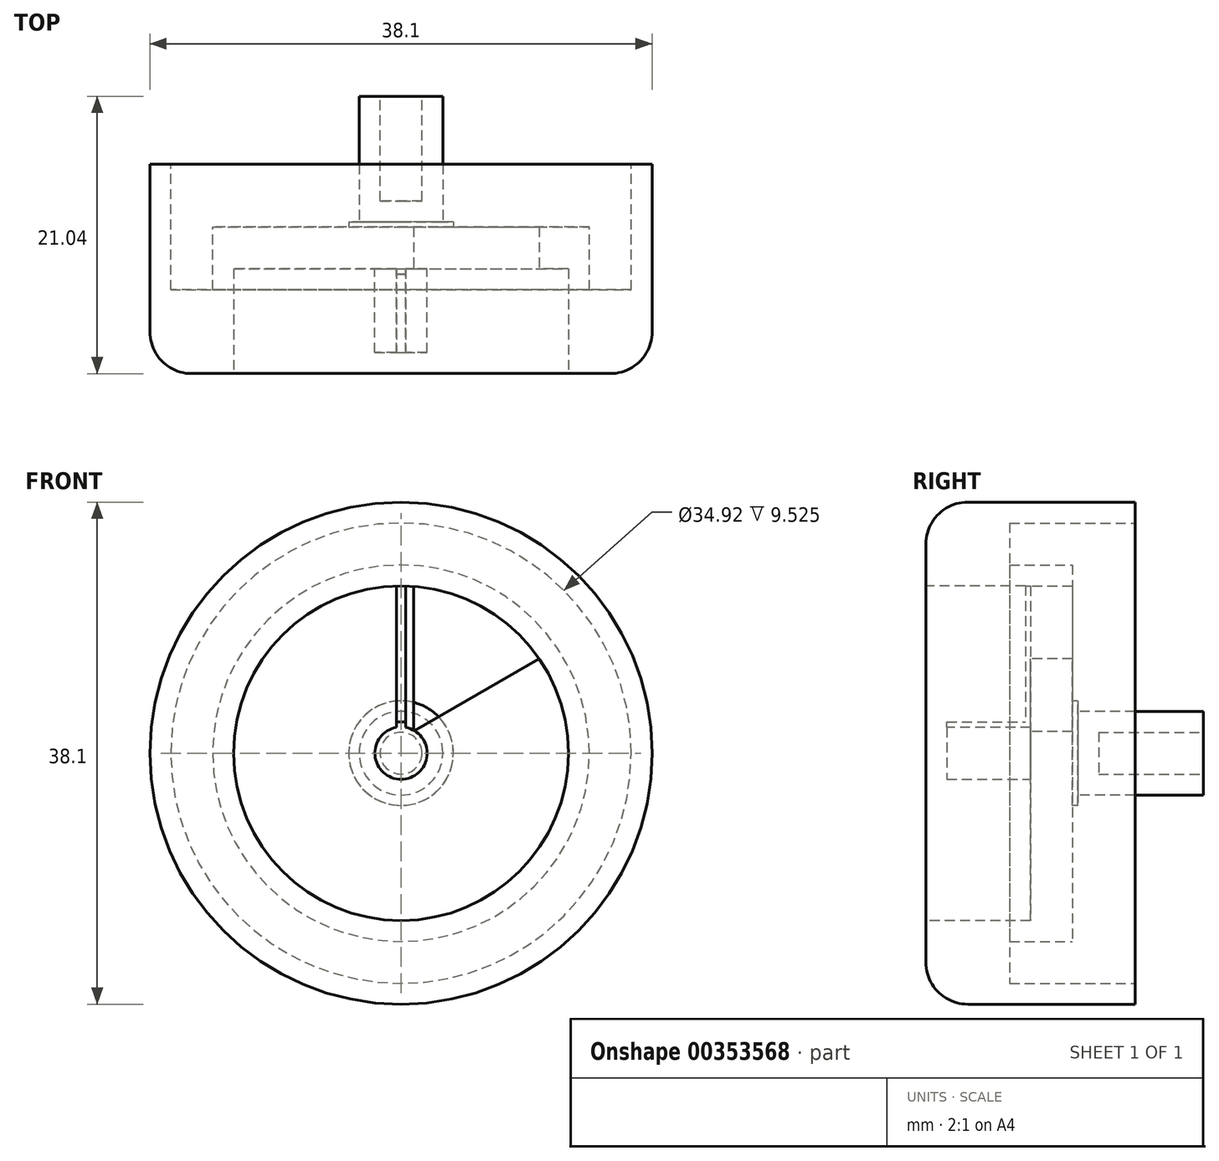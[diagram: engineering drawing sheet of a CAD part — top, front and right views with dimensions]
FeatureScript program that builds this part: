
annotation { "Feature Type Name" : "Feature", "Feature Type Description" : "" }
export const myFeature = defineFeature(function(context is Context, id is Id, definition is map)
    precondition{}
    {
        {
            var Q0;
            Q0=qCreatedBy(makeId("Front.planeOp"),FACE);
            var sketch = newSketch(context, id + "F0", { "sketchPlane" : qUnion([Q0])});
            skCircle(sketch, "E0", {"center": v(0, 0) * mm, "radius": 19.05 * mm});
            skSolve(sketch);
        }
        {
            var Q0;
            Q0 = qSketchRegion(id + "F0", true);
            extrude(context, id + "F1", {"entities" : qUnion([Q0]), "depth" : 15.88 * mm, "symmetric" : true});
        }
        {
            var Q0;
            Q0=makeQuery(id+"F1.opExtrude","CAP_FACE",FACE,{"disambiguationData":[OSD([sQuery(id+"F0.wireOp",EDGE,"E0")])],"isStart":false});
            var sketch = newSketch(context, id + "F2", { "sketchPlane" : qUnion([Q0])});
            skCircle(sketch, "E1", {"center": v(0, 0) * mm, "radius": 12.7 * mm});
            skSolve(sketch);
        }
        {
            var Q0;
            Q0 = qSketchRegion(id + "F2", true);
            extrude(context, id + "F3", {"entities" : qUnion([Q0]), "operationType" : NewBodyOperationType.REMOVE, "oppositeDirection" : true, "depth" : 7.94 * mm});
        }
        {
            var Q0;
            Q0=makeQuery(id+"F3.boolean.opBoolean","COPY",FACE,{"derivedFrom":makeQuery(id+"F3.opExtrude","CAP_FACE",FACE,{"disambiguationData":[OSD([sQuery(id+"F2.wireOp",EDGE,"E1")])],"isStart":false})});
            var sketch = newSketch(context, id + "F4", { "sketchPlane" : qUnion([Q0])});
            skLineSegment(sketch, "E2", {"start": v(0, 13.75) * mm, "end": v(0, 0) * mm, "construction": true});
            skLineSegment(sketch, "E3", {"start": v(0, 0) * mm, "end": v(12.12, 7) * mm, "construction": true});
            skLineSegment(sketch, "E4", {"start": v(0.95, 12.66) * mm, "end": v(0.95, 1.65) * mm});
            skLineSegment(sketch, "E5", {"start": v(0.95, 1.65) * mm, "end": v(10.5, 7.16) * mm});
            skArc(sketch, "E6.0", {"start": v(10.5, 7.16) * mm, "mid": v(6.35, 11) * mm, "end": v(0.95, 12.66) * mm});
            skLineSegment(sketch, "E7", {"start": v(0, 0) * mm, "end": v(9.55, 16.55) * mm, "construction": true});
            skSolve(sketch);
        }
        {
            var Q0;
            Q0 = qSketchRegion(id + "F4", true);
            extrude(context, id + "F5", {"entities" : qUnion([Q0]), "operationType" : NewBodyOperationType.REMOVE, "endBound" : BoundingType.THROUGH_ALL, "oppositeDirection" : true, "depth" : 25.4 * mm});
        }
        {
            var Q0;
            Q0=makeQuery(id+"F1.opExtrude","CAP_FACE",FACE,{"disambiguationData":[OSD([sQuery(id+"F0.wireOp",EDGE,"E0")])],"isStart":true});
            var sketch = newSketch(context, id + "F6", { "sketchPlane" : qUnion([Q0])});
            skCircle(sketch, "E8", {"center": v(0, 0) * mm, "radius": 12.7 * mm});
            skSolve(sketch);
        }
        {
            var Q0;
            Q0 = qSketchRegion(id + "F6", true);
            extrude(context, id + "F7", {"entities" : qUnion([Q0]), "operationType" : NewBodyOperationType.REMOVE, "oppositeDirection" : true, "depth" : 4.76 * mm});
        }
        {
            var Q0;
            Q0=makeQuery(id+"F7.boolean.opBoolean","COPY",FACE,{"derivedFrom":makeQuery(id+"F7.opExtrude","CAP_FACE",FACE,{"disambiguationData":[OSD([sQuery(id+"F6.wireOp",EDGE,"E8")])],"isStart":false})});
            var sketch = newSketch(context, id + "F8", { "sketchPlane" : qUnion([Q0])});
            skCircle(sketch, "E9", {"center": v(0, 0) * mm, "radius": 3.97 * mm});
            skSolve(sketch);
        }
        {
            var Q0;
            Q0 = qSketchRegion(id + "F8", true);
            extrude(context, id + "F9", {"entities" : qUnion([Q0]), "operationType" : NewBodyOperationType.ADD, "depth" : 0.4 * mm});
        }
        {
            var Q0;
            Q0=makeQuery(id+"F9.opExtrude","CAP_FACE",FACE,{"disambiguationData":[OSD([sQuery(id+"F8.wireOp",EDGE,"E9")])],"isStart":false});
            var sketch = newSketch(context, id + "F10", { "sketchPlane" : qUnion([Q0])});
            skCircle(sketch, "E10", {"center": v(0, 0) * mm, "radius": 3.17 * mm});
            skSolve(sketch);
        }
        {
            var Q0;
            Q0 = qSketchRegion(id + "F10", true);
            extrude(context, id + "F11", {"entities" : qUnion([Q0]), "operationType" : NewBodyOperationType.ADD, "depth" : 9.52 * mm});
        }
        {
            var Q0;
            Q0=makeQuery(id+"F11.opExtrude","CAP_FACE",FACE,{"disambiguationData":[OSD([sQuery(id+"F10.wireOp",EDGE,"E10")])],"isStart":false});
            var sketch = newSketch(context, id + "F12", { "sketchPlane" : qUnion([Q0])});
            skCircle(sketch, "E11", {"center": v(0, 0) * mm, "radius": 1.59 * mm});
            skSolve(sketch);
        }
        {
            var Q0;
            Q0 = qSketchRegion(id + "F12", true);
            extrude(context, id + "F13", {"entities" : qUnion([Q0]), "operationType" : NewBodyOperationType.REMOVE, "oppositeDirection" : true, "depth" : 7.94 * mm});
        }
        {
            var Q0;
            Q0=makeQuery(id+"F3.boolean.opBoolean","COPY",FACE,{"derivedFrom":makeQuery(id+"F3.opExtrude","CAP_FACE",FACE,{"disambiguationData":[OSD([sQuery(id+"F2.wireOp",EDGE,"E1")])],"isStart":false})});
            var sketch = newSketch(context, id + "F14", { "sketchPlane" : qUnion([Q0])});
            skCircle(sketch, "E12", {"center": v(0, 0) * mm, "radius": 1.98 * mm});
            skSolve(sketch);
        }
        {
            var Q0;
            Q0 = qSketchRegion(id + "F14", true);
            extrude(context, id + "F15", {"entities" : qUnion([Q0]), "operationType" : NewBodyOperationType.ADD, "depth" : 6.35 * mm});
        }
        {
            var Q0;
            {var subQ2=sQuery(id+"F2.wireOp",EDGE,"E1");Q0=makeQuery(id+"F15.boolean.opBoolean","SPLIT",FACE,{"disambiguationData":[TD([makeQuery(id+"F5.boolean.opBoolean","COPY",FACE,{"derivedFrom":makeQuery(id+"F5.opExtrude","SWEPT_FACE",FACE,{"disambiguationData":[OSD([sQuery(id+"F4.wireOp",EDGE,"E4")])]})})])],"derivedFrom":makeQuery(id+"F3.boolean.opBoolean","COPY",FACE,{"derivedFrom":makeQuery(id+"F3.opExtrude","CAP_FACE",FACE,{"disambiguationData":[OSD([subQ2])],"isStart":false})})});}
            var sketch = newSketch(context, id + "F16", { "sketchPlane" : qUnion([Q0])});
            skLineSegment(sketch, "E13.bottom", {"start": v(-0.34, 12.7) * mm, "end": v(0.34, 12.7) * mm});
            skLineSegment(sketch, "E13.top", {"start": v(-0.34, 2.37) * mm, "end": v(0.34, 2.37) * mm});
            skLineSegment(sketch, "E13.left", {"start": v(-0.34, 12.7) * mm, "end": v(-0.34, 2.37) * mm});
            skLineSegment(sketch, "E13.right", {"start": v(0.34, 12.7) * mm, "end": v(0.34, 2.37) * mm});
            skSolve(sketch);
        }
        {
            var Q0;
            {var subQ0=sQuery(id+"F16.wireOp",EDGE,"E13.left");var subQ1=sQuery(id+"F16.wireOp",EDGE,"E13.top");var subQ2=makeQuery(id+"F16.imprint","INTERSECT",VERTEX,{"derivedFrom":[subQ1,subQ0]});Q0=makeQuery(id+"F16.imprint","IMPRINT",FACE,{"disambiguationData":[TD([[makeQuery(id+"F16.imprint","IMPRINT",EDGE,{"disambiguationData":[TD([[subQ2,-1.0]])],"derivedFrom":subQ1}),1.0]])]});}
            extrude(context, id + "F17", {"entities" : qUnion([Q0]), "operationType" : NewBodyOperationType.ADD, "depth" : 0.4 * mm});
        }
        {
            var Q0;
            Q0=makeQuery(id+"F15.opExtrude","CAP_FACE",FACE,{"disambiguationData":[OSD([sQuery(id+"F14.wireOp",EDGE,"E12")])],"isStart":false});
            var sketch = newSketch(context, id + "F18", { "sketchPlane" : qUnion([Q0])});
            skLineSegment(sketch, "E14.bottom", {"start": v(-0.34, 1.95) * mm, "end": v(0.34, 1.95) * mm});
            skLineSegment(sketch, "E14.top", {"start": v(-0.34, 2.36) * mm, "end": v(0.34, 2.36) * mm});
            skLineSegment(sketch, "E14.left", {"start": v(-0.34, 1.95) * mm, "end": v(-0.34, 2.36) * mm});
            skLineSegment(sketch, "E14.right", {"start": v(0.34, 1.95) * mm, "end": v(0.34, 2.36) * mm});
            skSolve(sketch);
        }
        {
            var Q0;
            Q0 = qSketchRegion(id + "F18", true);
            extrude(context, id + "F19", {"entities" : qUnion([Q0]), "operationType" : NewBodyOperationType.ADD, "oppositeDirection" : true, "depth" : 6.35 * mm});
        }
        {
            var Q0;
            Q0=makeQuery(id+"F1.opExtrude","CAP_FACE",FACE,{"disambiguationData":[OSD([sQuery(id+"F0.wireOp",EDGE,"E0")])],"isStart":true});
            var sketch = newSketch(context, id + "F20", { "sketchPlane" : qUnion([Q0])});
            skCircle(sketch, "E15", {"center": v(0, 0) * mm, "radius": 17.46 * mm});
            skSolve(sketch);
        }
        {
            var Q0;
            Q0=makeQuery(id+"F20.imprint","IMPRINT",FACE,{"disambiguationData":[TD([[makeQuery(id+"F20.imprint","IMPRINT",EDGE,{"derivedFrom":sQuery(id+"F20.wireOp",EDGE,"E15")}),1.0]])]});
            var sketch = newSketch(context, id + "F21", { "sketchPlane" : qUnion([Q0])});
            skCircle(sketch, "E16.0", {"center": v(0, 0) * mm, "radius": 12.7 * mm});
            skCircle(sketch, "E17.0", {"center": v(0, 0) * mm, "radius": 17.46 * mm});
            skSolve(sketch);
        }
        {
            var Q0;
            Q0 = qSketchRegion(id + "F21", true);
            var Q1;
            Q1=makeQuery(id+"F20.imprint","IMPRINT",FACE,{"disambiguationData":[TD([[makeQuery(id+"F20.imprint","IMPRINT",EDGE,{"derivedFrom":sQuery(id+"F20.wireOp",EDGE,"E15")}),1.0]])]});
            var Q2;
            {var subQ2=sQuery(id+"F6.wireOp",EDGE,"E8");Q2=makeQuery(id+"F9.boolean.opBoolean","SPLIT",FACE,{"disambiguationData":[TD([makeQuery(id+"FinYMH1RS6XASPV_1.4.F5.boolean.opBoolean","COPY",FACE,{"derivedFrom":makeQuery(id+"FinYMH1RS6XASPV_1.4.F5.opExtrude","SWEPT_FACE",FACE,{"disambiguationData":[OSD([sQuery(id+"F4.wireOp",EDGE,"E5")])]})})])],"derivedFrom":makeQuery(id+"F7.boolean.opBoolean","COPY",FACE,{"derivedFrom":makeQuery(id+"F7.opExtrude","CAP_FACE",FACE,{"disambiguationData":[OSD([subQ2])],"isStart":false})})});}
            extrude(context, id + "F22", {"entities" : qUnion([Q0, Q1]), "operationType" : NewBodyOperationType.REMOVE, "endBound" : BoundingType.UP_TO_SURFACE, "oppositeDirection" : true, "endBoundEntityFace" : qUnion([Q2]), "depth" : 25.4 * mm});
        }
        {
            var Q0;
            {var subQ4=sQuery(id+"F4.wireOp",EDGE,"E5");var subQ9=sQuery(id+"F6.wireOp",EDGE,"E8");var subQ11=sQuery(id+"F4.wireOp",EDGE,"E4");var subQ15=makeQuery(id+"F7.boolean.opBoolean","COPY",FACE,{"derivedFrom":makeQuery(id+"F7.opExtrude","CAP_FACE",FACE,{"disambiguationData":[OSD([subQ9])],"isStart":false})});Q0=makeQuery(id+"F22.boolean.opBoolean","MERGE",FACE,{"derivedFrom":[makeQuery(id+"F9.boolean.opBoolean","SPLIT",FACE,{"disambiguationData":[TD([makeQuery(id+"F5.boolean.opBoolean","COPY",FACE,{"derivedFrom":makeQuery(id+"F5.opExtrude","SWEPT_FACE",FACE,{"disambiguationData":[OSD([subQ11])]})})])],"derivedFrom":subQ15}),makeQuery(id+"F9.boolean.opBoolean","SPLIT",FACE,{"disambiguationData":[TD([makeQuery(id+"F5.boolean.opBoolean","COPY",FACE,{"derivedFrom":makeQuery(id+"F5.opExtrude","SWEPT_FACE",FACE,{"disambiguationData":[OSD([subQ4])]})})])],"derivedFrom":subQ15}),makeQuery(id+"F9.boolean.opBoolean","SPLIT",FACE,{"disambiguationData":[TD([makeQuery(id+"FinYMH1RS6XASPV_1.1.F5.boolean.opBoolean","COPY",FACE,{"derivedFrom":makeQuery(id+"FinYMH1RS6XASPV_1.1.F5.opExtrude","SWEPT_FACE",FACE,{"disambiguationData":[OSD([subQ4])]})})])],"derivedFrom":subQ15}),makeQuery(id+"F9.boolean.opBoolean","SPLIT",FACE,{"disambiguationData":[TD([makeQuery(id+"FinYMH1RS6XASPV_1.2.F5.boolean.opBoolean","COPY",FACE,{"derivedFrom":makeQuery(id+"FinYMH1RS6XASPV_1.2.F5.opExtrude","SWEPT_FACE",FACE,{"disambiguationData":[OSD([subQ4])]})})])],"derivedFrom":subQ15}),makeQuery(id+"F9.boolean.opBoolean","SPLIT",FACE,{"disambiguationData":[TD([makeQuery(id+"FinYMH1RS6XASPV_1.3.F5.boolean.opBoolean","COPY",FACE,{"derivedFrom":makeQuery(id+"FinYMH1RS6XASPV_1.3.F5.opExtrude","SWEPT_FACE",FACE,{"disambiguationData":[OSD([subQ4])]})})])],"derivedFrom":subQ15}),makeQuery(id+"F9.boolean.opBoolean","SPLIT",FACE,{"disambiguationData":[TD([makeQuery(id+"FinYMH1RS6XASPV_1.4.F5.boolean.opBoolean","COPY",FACE,{"derivedFrom":makeQuery(id+"FinYMH1RS6XASPV_1.4.F5.opExtrude","SWEPT_FACE",FACE,{"disambiguationData":[OSD([subQ4])]})})])],"derivedFrom":subQ15}),makeQuery(id+"F22.opExtrude","CAP_FACE",FACE,{"disambiguationData":[OSD([sQuery(id+"F21.wireOp",EDGE,"E16.0"),sQuery(id+"F21.wireOp",EDGE,"E17.0")])],"isStart":false})]});}
            var sketch = newSketch(context, id + "F23", { "sketchPlane" : qUnion([Q0])});
            skCircle(sketch, "E18", {"center": v(0, 0) * mm, "radius": 14.29 * mm});
            skSolve(sketch);
        }
        {
            var Q0;
            Q0=makeQuery(id+"F23.imprint","IMPRINT",FACE,{"disambiguationData":[TD([[makeQuery(id+"F23.imprint","IMPRINT",EDGE,{"derivedFrom":sQuery(id+"F23.wireOp",EDGE,"E18")}),-1.0]])]});
            var sketch = newSketch(context, id + "F24", { "sketchPlane" : qUnion([Q0])});
            skCircle(sketch, "E19.0", {"center": v(0, 0) * mm, "radius": 14.29 * mm});
            skCircle(sketch, "E20.0", {"center": v(0, 0) * mm, "radius": 17.46 * mm});
            skSolve(sketch);
        }
        {
            var Q0;
            Q0 = qSketchRegion(id + "F24", true);
            extrude(context, id + "F25", {"entities" : qUnion([Q0]), "operationType" : NewBodyOperationType.REMOVE, "oppositeDirection" : true, "depth" : 4.76 * mm});
        }
        {
            var Q0;
            Q0=makeQuery(id+"F1.opExtrude","CAP_EDGE",EDGE,{"disambiguationData":[OSD([sQuery(id+"F0.wireOp",EDGE,"E0")])],"isStart":false});
            var Q1;
            Q1=makeQuery(id+"F3.boolean.opBoolean","COPY",EDGE,{"derivedFrom":makeQuery(id+"F3.opExtrude","CAP_EDGE",EDGE,{"disambiguationData":[OSD([sQuery(id+"F2.wireOp",EDGE,"E1")])],"isStart":true})});
            fillet(context, id + "F26", {"entities" : qUnion([Q0, Q1]), "radius" : 3.17 * mm, "tangentPropagation" : true, "allowEdgeOverflow" : false});
        }
    });
